# Revit family: Faucet-Single_Handle-American_Standard-Saybrook-4902330_Series
name_source: partatom
category: Plumbing Fixtures
units: mm (PartAtom-declared; Revit-internal decimal feet)

## family parameters
Always vertical = No
Cut with Voids When Loaded = No
OmniClass Number = 23.45.55.14
OmniClass Title = Single Faucets
Part Type = Normal
Room Calculation Point = No
Round Connector Dimension = Use Diameter
Shared = Yes
Work Plane-Based = Yes

## types (2) — shared parameters
ADA Compliant = Yes
Above Deck Filter = No
Assembly Code = D2020300
CEC Compliant = Yes
CW Connection = No
CWFU = 1.5
CalGreen Compliant = Yes
Default Elevation = 0"
Description = Saybrook Single-Handle Pull-Down Dual Spray Kitchen Faucet 1.5 GPM with Filter
Escutcheon Plate = No
Filter Life = 300 gal.
Flow Rate = 1.5 gpm (5.7 L/min)
HW Connection = No
HWFU = 1.5
Height = 18 15/16"
IAPMO Compliance = Meet or exceeds ANSI A117.1AS ME A112 .18 .1CSA B12 5 .1NSF 61/Section 9NSF 372NSF 42 for the reduction of chlorine, taste & odor, and particulate, class INSF 53 for the reduction of leadDOE / CEC / cUPC
Installation Type = Deck Mounted
Length = 10 5/8"
Manufacturer = American Standard
Price = Prices may vary. Please consult Manufacturer Representative for most up-to-date price list.
Product Documentation Link = https://americanstandard.box.com
Product Page URL = https://www.americanstandard-us.com
Tempered Water Connection = Yes
Tempered Water Connection Diameter = 1/2"
Tempered Water Connection Radius = 1/4"
URL = https://www.americanstandard-us.com
Vent Connection = No
WFU = 2
Warranty Information = Limited Lifetime Guarantee
Waste Connection = No
Width = 10 7/16"
cUPC Compliant = Yes

## per-type parameters (varying)
| type | Finish | Material |
| 4902330.002 | Metal-American Standard-002-Polished Chrome | Metal-American Standard-002-Polished Chrome |
| 4902330.075 | Metal-American Standard-075-Stainless Steel | Metal-American Standard-075-Stainless Steel |

note: column(s) folded — value = type name in every type: Model

## geometry (parser evidence)
native form markers: Sweep x2
no freeform markers — native parametric forms only
